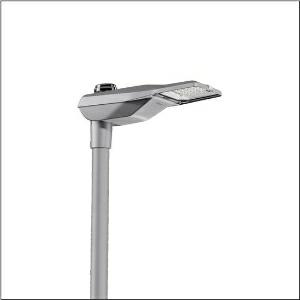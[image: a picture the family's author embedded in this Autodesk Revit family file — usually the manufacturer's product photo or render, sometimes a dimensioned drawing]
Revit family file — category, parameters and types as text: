
# Revit family: streetlight_sl_21_micro___p0_8a_5xe5u67n08cb_86d2
name_source: partatom
category: Lighting Fixtures
units: mm (PartAtom-declared; Revit-internal decimal feet)

## family parameters
Cut with Voids When Loaded = No
Host = Face
Light Source = No
Part Type = Normal
Room Calculation Point = No
Round Connector Dimension = Use Diameter
Shared = No

## types (1)
- --- (1 x LED, 2020 lm, 15.8 W, 2700K)
    Apparent Load = 16 VA
    CIE Flux Codes = 33 69 96 100 100
    Color Rendering = 70
    Color Temperature = 2700K
    Default Elevation = 1800 mm
    Description = Streetlight SL 21 micro, mast luminaire, primary light control with lens, of PMMA, primary optical cover: cover, of toughened safety glass, transparent, light distribution: P0.8a, light emission: direct distribution, primary light characteristic: asymmetric, installation type: post-top, LED, 3G 1.5mm², High Power LED, rated luminous flux: 2.020lm, luminous efficacy: 128lm/W, light colour: 727, colour temperature: 2700K, control gear: NEMA (7pin), control: flexible luminous flux parameterisation, time-dependent luminous flux control, constant luminous flux control, pre-setting: linear dimming characteristic, overheat protection, mains connection: 230..240V, AC, 50/60Hz, connection cable pre-assembled, cable length: 6,5m, wiring characteristics: H07RN-F, start of lifetime: 16W, end of service life: 16W, reduction: 8W, luminaire housing, of diecast aluminium (EN AC-44300), powder-coated, Siteco® metallic grey (DB 702S), corrosivity category C5 mid according to DIN EN ISO 12944, multi-level sealing system, sealing non-destructively replaceable, inclination adjustable: 0°, 5°, 10°, 15°, length: 528mm, width: 235mm, height: 110mm, spigot size: 76/60mm (post-top), mounting height: 4..8m, protection rating (complete): IP66, insulation class (complete): insulation class I (protective earthing), certification: CE, ENEC, ENEC+, VDE, impact resistance: IK10, permissible operating ambient temperature for outdoor applications: -40..+50°C, standard-compliant lighting for roads and squares, packaging unit: 1 piece

Light Distribution: P0.8a
    Height = 110 mm
    Lamp = 1 x LED
    Lamp Light Flux = 2020 lm
    Lamp Power = 15.8 W
    Lamp count = 1
    Length = 528 mm
    Luminous efficacy = 128 lm/W
    Manufacturer = Siteco
    ModVariant = No
    Model = 5XE5U67N08CB
    Number of Poles = 1
    OnlyDefault = Yes
    Power Factor = 1
    Product Name = Streetlight SL 21 micro | P0.8a
    Product group = mast luminaire | pylon top
    ProductGroupID = 6100
    Protection Class = Protection class I
    Protection Degree = IP 66
    RLX_Detail_Level = 1
    RLX_Emergency_Light_Flux = 0 lm
    RLX_Emergency_Type = 0
    RLX_Emergency_Type_DB = No
    RlxData = <blob elided: 99013 chars, md5=924dc0a5>
    Socket = socket
    Standby Power = 0 W
    System Light Flux = 2020 lm
    System Power = 16 W
    Type Comments = factory setting: luminous flux: 100 % | dim-lin: 254 | 300 mA
    Type Image = l_1294375.jpg
    URL = http://relux.com
    VarID = @adj_073698
    Voltage = 0 V
    Weight = 0.00 kg
    Width = 235 mm

## geometry (parser evidence)
native form markers: Blend x4, Sweep x9
no freeform markers — native parametric forms only
